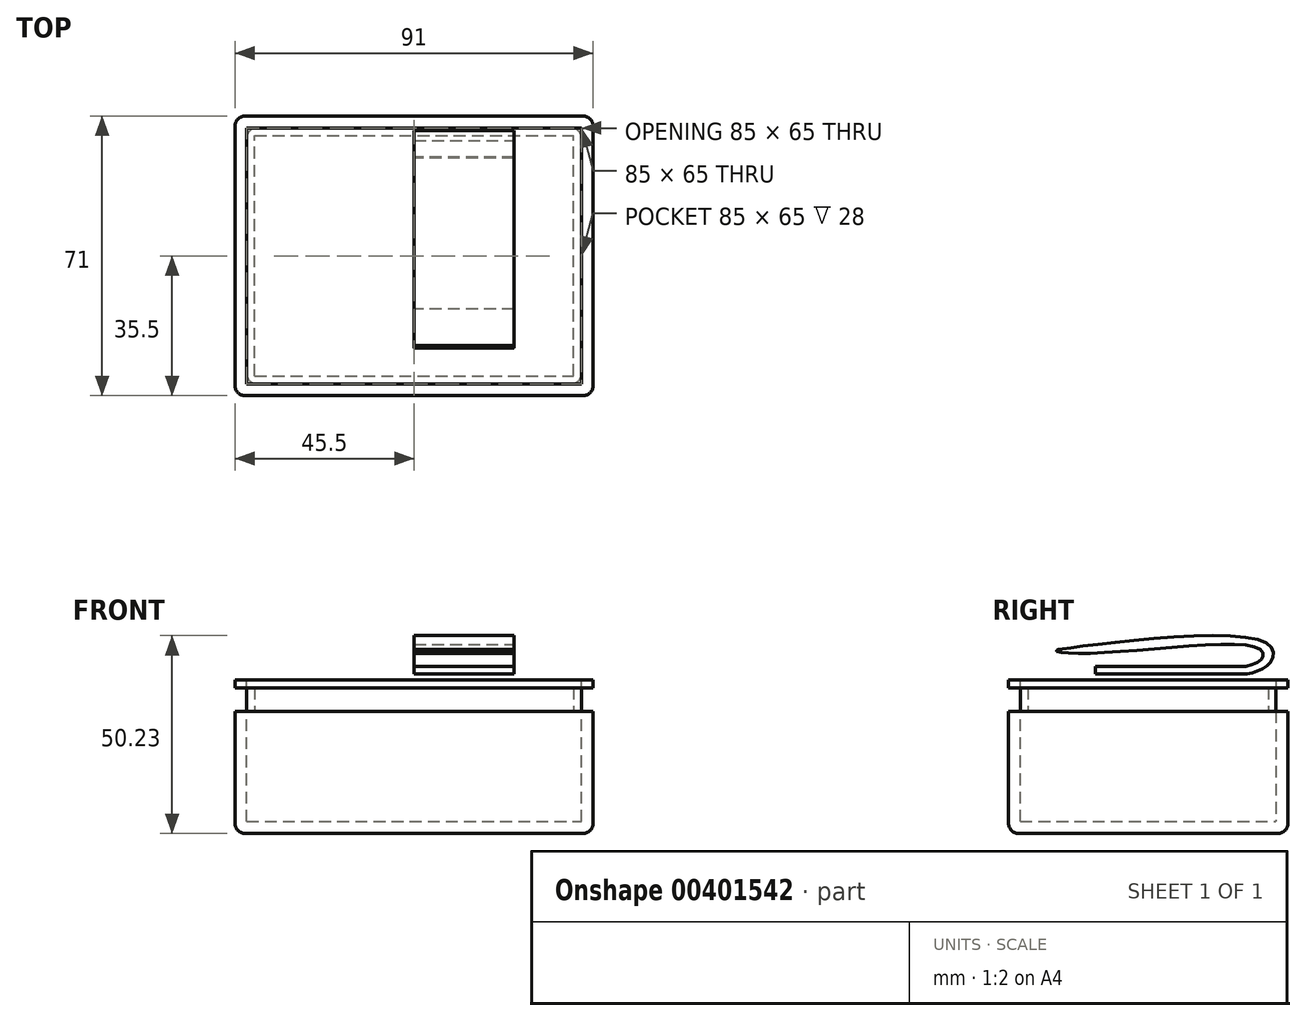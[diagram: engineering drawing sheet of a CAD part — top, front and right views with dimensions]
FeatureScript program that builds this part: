
annotation { "Feature Type Name" : "Feature", "Feature Type Description" : "" }
export const myFeature = defineFeature(function(context is Context, id is Id, definition is map)
    precondition{}
    {
        {
            var Q0;
            Q0=qCreatedBy(makeId("Top.planeOp"),FACE);
            var sketch = newSketch(context, id + "F0", { "sketchPlane" : qUnion([Q0])});
            skLineSegment(sketch, "E0.bottom", {"start": v(-45.5, 35.5) * mm, "end": v(45.5, 35.5) * mm});
            skLineSegment(sketch, "E0.top", {"start": v(-45.5, -35.5) * mm, "end": v(45.5, -35.5) * mm});
            skLineSegment(sketch, "E0.left", {"start": v(-45.5, 35.5) * mm, "end": v(-45.5, -35.5) * mm});
            skLineSegment(sketch, "E0.right", {"start": v(45.5, 35.5) * mm, "end": v(45.5, -35.5) * mm});
            skPoint(sketch, "E0.middle", {"position": v(0, 0) * mm});
            skSolve(sketch);
        }
        {
            var Q0;
            Q0 = qSketchRegion(id + "F0", true);
            extrude(context, id + "F1", {"entities" : qUnion([Q0]), "depth" : 39 * mm});
        }
        {
            var Q0;
            Q0=makeQuery(id+"F1.opExtrude","CAP_EDGE",EDGE,{"disambiguationData":[OSD([sQuery(id+"F0.wireOp",EDGE,"E0.top")])],"isStart":true});
            var Q1;
            Q1=makeQuery(id+"F1.opExtrude","SWEPT_EDGE",EDGE,{"disambiguationData":[OSD([sQuery(id+"F0.wireOp",EDGE,"E0.top"),sQuery(id+"F0.wireOp",EDGE,"E0.right")])]});
            var Q2;
            Q2=makeQuery(id+"F1.opExtrude","CAP_EDGE",EDGE,{"disambiguationData":[OSD([sQuery(id+"F0.wireOp",EDGE,"E0.right")])],"isStart":true});
            var Q3;
            Q3=makeQuery(id+"F1.opExtrude","CAP_EDGE",EDGE,{"disambiguationData":[OSD([sQuery(id+"F0.wireOp",EDGE,"E0.bottom")])],"isStart":true});
            var Q4;
            Q4=makeQuery(id+"F1.opExtrude","SWEPT_EDGE",EDGE,{"disambiguationData":[OSD([sQuery(id+"F0.wireOp",EDGE,"E0.bottom"),sQuery(id+"F0.wireOp",EDGE,"E0.right")])]});
            var Q5;
            Q5=makeQuery(id+"F1.opExtrude","CAP_EDGE",EDGE,{"disambiguationData":[OSD([sQuery(id+"F0.wireOp",EDGE,"E0.left")])],"isStart":true});
            var Q6;
            Q6=makeQuery(id+"F1.opExtrude","SWEPT_EDGE",EDGE,{"disambiguationData":[OSD([sQuery(id+"F0.wireOp",EDGE,"E0.bottom"),sQuery(id+"F0.wireOp",EDGE,"E0.left")])]});
            var Q7;
            Q7=makeQuery(id+"F1.opExtrude","SWEPT_EDGE",EDGE,{"disambiguationData":[OSD([sQuery(id+"F0.wireOp",EDGE,"E0.top"),sQuery(id+"F0.wireOp",EDGE,"E0.left")])]});
            fillet(context, id + "F2", {"entities" : qUnion([Q0, Q1, Q2, Q3, Q4, Q5, Q6, Q7]), "radius" : 2.54 * mm, "tangentPropagation" : true, "allowEdgeOverflow" : false});
        }
        {
            var Q0;
            Q0=makeQuery(id+"F1.opExtrude","CAP_FACE",FACE,{"disambiguationData":[OSD([sQuery(id+"F0.wireOp",EDGE,"E0.bottom"),sQuery(id+"F0.wireOp",EDGE,"E0.top"),sQuery(id+"F0.wireOp",EDGE,"E0.left"),sQuery(id+"F0.wireOp",EDGE,"E0.right")])],"isStart":false});
            shell(context, id + "F3", {"entities" : qUnion([Q0]), "thickness" : 3 * mm});
        }
        {
            var Q0;
            Q0=makeQuery(id+"F1.opExtrude","CAP_FACE",FACE,{"disambiguationData":[OSD([sQuery(id+"F0.wireOp",EDGE,"E0.bottom"),sQuery(id+"F0.wireOp",EDGE,"E0.top"),sQuery(id+"F0.wireOp",EDGE,"E0.left"),sQuery(id+"F0.wireOp",EDGE,"E0.right")])],"isStart":false});
            var sketch = newSketch(context, id + "F4", { "sketchPlane" : qUnion([Q0])});
            skLineSegment(sketch, "E1.bottom", {"start": v(-42.96, 35.5) * mm, "end": v(42.96, 35.5) * mm});
            skLineSegment(sketch, "E1.top", {"start": v(-42.96, -35.5) * mm, "end": v(42.96, -35.5) * mm});
            skLineSegment(sketch, "E1.left", {"start": v(-45.5, 32.96) * mm, "end": v(-45.5, -32.96) * mm});
            skLineSegment(sketch, "E1.right", {"start": v(45.5, 32.96) * mm, "end": v(45.5, -32.96) * mm});
            skPoint(sketch, "E1.middle", {"position": v(0, 0) * mm});
            skPoint(sketch, "E2.visualSharp", {"position": v(-45.5, 35.5) * mm});
            skArc(sketch, "E2.filletArc", {"start": v(-42.96, 35.5) * mm, "mid": v(-44.76, 34.76) * mm, "end": v(-45.5, 32.96) * mm});
            skPoint(sketch, "E3.visualSharp", {"position": v(45.5, 35.5) * mm});
            skArc(sketch, "E3.filletArc", {"start": v(45.5, 32.96) * mm, "mid": v(44.76, 34.76) * mm, "end": v(42.96, 35.5) * mm});
            skPoint(sketch, "E4.visualSharp", {"position": v(45.5, -35.5) * mm});
            skArc(sketch, "E4.filletArc", {"start": v(42.96, -35.5) * mm, "mid": v(44.76, -34.76) * mm, "end": v(45.5, -32.96) * mm});
            skPoint(sketch, "E5.visualSharp", {"position": v(-45.5, -35.5) * mm});
            skArc(sketch, "E5.filletArc", {"start": v(-45.5, -32.96) * mm, "mid": v(-44.76, -34.76) * mm, "end": v(-42.96, -35.5) * mm});
            skSolve(sketch);
        }
        {
            var Q0;
            Q0 = qSketchRegion(id + "F4", true);
            extrude(context, id + "F5", {"entities" : qUnion([Q0]), "oppositeDirection" : true, "depth" : 8 * mm});
        }
        {
            var Q0;
            Q0=makeQuery(id+"F5.opExtrude","CAP_FACE",FACE,{"disambiguationData":[OSD([sQuery(id+"F4.wireOp",EDGE,"E1.bottom"),sQuery(id+"F4.wireOp",EDGE,"E1.top"),sQuery(id+"F4.wireOp",EDGE,"E1.left"),sQuery(id+"F4.wireOp",EDGE,"E1.right"),sQuery(id+"F4.wireOp",EDGE,"E2.filletArc"),sQuery(id+"F4.wireOp",EDGE,"E3.filletArc"),sQuery(id+"F4.wireOp",EDGE,"E4.filletArc"),sQuery(id+"F4.wireOp",EDGE,"E5.filletArc")])],"isStart":false});
            var sketch = newSketch(context, id + "F6", { "sketchPlane" : qUnion([Q0])});
            skLineSegment(sketch, "E6.bottom", {"start": v(-42.5, 32.5) * mm, "end": v(42.5, 32.5) * mm});
            skLineSegment(sketch, "E6.top", {"start": v(-42.5, -32.5) * mm, "end": v(42.5, -32.5) * mm});
            skLineSegment(sketch, "E6.left", {"start": v(-42.5, 32.5) * mm, "end": v(-42.5, -32.5) * mm});
            skLineSegment(sketch, "E6.right", {"start": v(42.5, 32.5) * mm, "end": v(42.5, -32.5) * mm});
            skPoint(sketch, "E6.middle", {"position": v(0, 0) * mm});
            skSolve(sketch);
        }
        {
            var Q0;
            Q0=makeQuery(id+"F6.imprint","IMPRINT",FACE,{"disambiguationData":[TD([[makeQuery(id+"F6.imprint","IMPRINT",EDGE,{"derivedFrom":sQuery(id+"F6.wireOp",EDGE,"E6.bottom")}),1.0]])]});
            extrude(context, id + "F7", {"entities" : qUnion([Q0]), "operationType" : NewBodyOperationType.REMOVE, "oppositeDirection" : true, "depth" : 6 * mm});
        }
        {
            var Q0;
            Q0=makeQuery(id+"F5.opExtrude","CAP_FACE",FACE,{"disambiguationData":[OSD([sQuery(id+"F4.wireOp",EDGE,"E1.bottom"),sQuery(id+"F4.wireOp",EDGE,"E1.top"),sQuery(id+"F4.wireOp",EDGE,"E1.left"),sQuery(id+"F4.wireOp",EDGE,"E1.right"),sQuery(id+"F4.wireOp",EDGE,"E2.filletArc"),sQuery(id+"F4.wireOp",EDGE,"E3.filletArc"),sQuery(id+"F4.wireOp",EDGE,"E4.filletArc"),sQuery(id+"F4.wireOp",EDGE,"E5.filletArc")])],"isStart":false});
            shell(context, id + "F8", {"entities" : qUnion([Q0]), "thickness" : 2 * mm});
        }
        {
            var Q0;
            Q0=makeQuery(id+"F7.boolean.opBoolean","COPY",EDGE,{"derivedFrom":makeQuery(id+"F7.opExtrude","SWEPT_EDGE",EDGE,{"disambiguationData":[OSD([sQuery(id+"F6.wireOp",EDGE,"E6.top"),sQuery(id+"F6.wireOp",EDGE,"E6.left")])]})});
            var Q1;
            Q1=makeQuery(id+"F7.boolean.opBoolean","COPY",EDGE,{"derivedFrom":makeQuery(id+"F7.opExtrude","SWEPT_EDGE",EDGE,{"disambiguationData":[OSD([sQuery(id+"F6.wireOp",EDGE,"E6.bottom"),sQuery(id+"F6.wireOp",EDGE,"E6.left")])]})});
            var Q2;
            Q2=makeQuery(id+"F7.boolean.opBoolean","COPY",EDGE,{"derivedFrom":makeQuery(id+"F7.opExtrude","SWEPT_EDGE",EDGE,{"disambiguationData":[OSD([sQuery(id+"F6.wireOp",EDGE,"E6.bottom"),sQuery(id+"F6.wireOp",EDGE,"E6.right")])]})});
            var Q3;
            Q3=makeQuery(id+"F7.boolean.opBoolean","COPY",EDGE,{"derivedFrom":makeQuery(id+"F7.opExtrude","SWEPT_EDGE",EDGE,{"disambiguationData":[OSD([sQuery(id+"F6.wireOp",EDGE,"E6.top"),sQuery(id+"F6.wireOp",EDGE,"E6.right")])]})});
            fillet(context, id + "F9", {"entities" : qUnion([Q0, Q1, Q2, Q3]), "radius" : 2.54 * mm, "tangentPropagation" : true, "allowEdgeOverflow" : false});
        }
        {
            var Q0;
            Q0=qCreatedBy(makeId("Right.planeOp"),FACE);
            var sketch = newSketch(context, id + "F10", { "sketchPlane" : qUnion([Q0])});
            skLineSegment(sketch, "E7", {"start": v(-13.45, 40.5) * mm, "end": v(25.04, 40.5) * mm});
            skFitSpline(sketch, "E8", {"points": [v(25.04, 40.5) * mm, v(30.98, 43.32) * mm, v(29.42, 48.73) * mm, v(-22.8, 46.72) * mm, v(-23.36, 46.44) * mm], "startDerivative": vector(33.74, 7.16) * mm, "endDerivative": vector(-27.67, -13.83) * mm});
            skLineSegment(sketch, "E9", {"start": v(-13.45, 40.5) * mm, "end": v(-13.45, 42.41) * mm});
            skLineSegment(sketch, "E10", {"start": v(-13.45, 42.41) * mm, "end": v(24.84, 42.41) * mm});
            skFitSpline(sketch, "E11", {"points": [v(24.84, 42.41) * mm, v(29.12, 44.77) * mm, v(27.6, 47.2) * mm, v(-12.83, 45.83) * mm, v(-23.36, 46.44) * mm, v(-22.8, 46.72) * mm], "startDerivative": vector(41.68, 10.18) * mm, "endDerivative": vector(2.87, 2.14) * mm});
            skSolve(sketch);
        }
        {
            var Q0;
            {var subQ4=sQuery(id+"F10.wireOp",EDGE,"E7");Q0=makeQuery(id+"F10.imprint","IMPRINT",FACE,{"disambiguationData":[TD([[makeQuery(id+"F10.imprint","IMPRINT",EDGE,{"derivedFrom":subQ4}),1.0]])]});}
            extrude(context, id + "F11", {"entities" : qUnion([Q0]), "depth" : 25.4 * mm});
        }
    });
